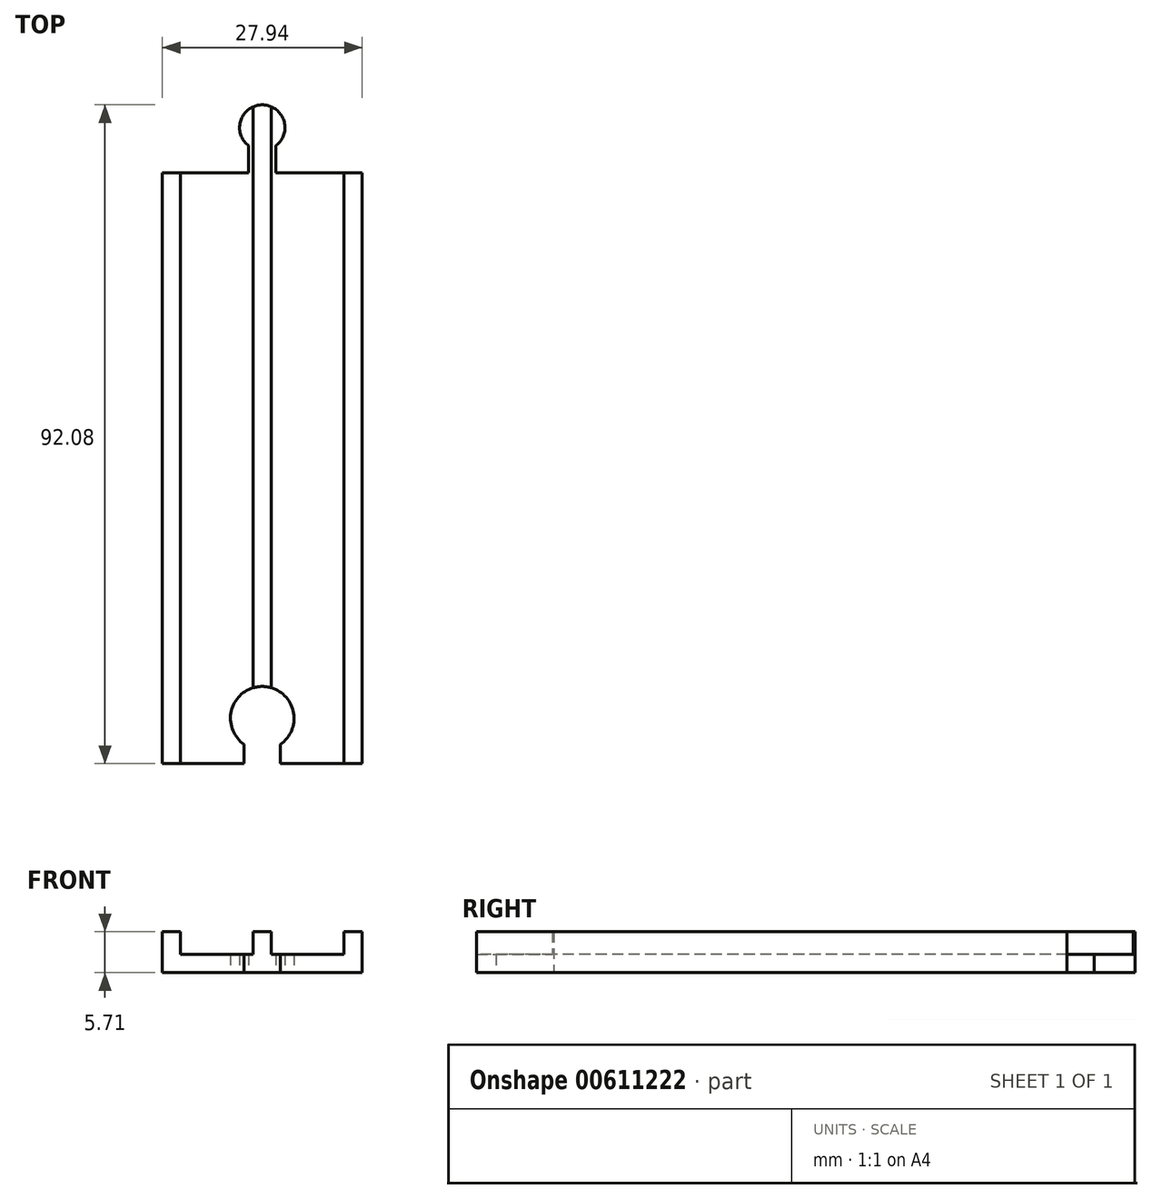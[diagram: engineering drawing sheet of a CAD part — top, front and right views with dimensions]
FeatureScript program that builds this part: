
annotation { "Feature Type Name" : "Feature", "Feature Type Description" : "" }
export const myFeature = defineFeature(function(context is Context, id is Id, definition is map)
    precondition{}
    {
        {
            var Q0;
            Q0=qCreatedBy(makeId("Top.planeOp"),FACE);
            var sketch = newSketch(context, id + "F0", { "sketchPlane" : qUnion([Q0])});
            skLineSegment(sketch, "E0.bottom", {"start": v(0, 0) * mm, "end": v(27.94, 0) * mm});
            skLineSegment(sketch, "E0.top", {"start": v(0, 82.55) * mm, "end": v(27.94, 82.55) * mm});
            skLineSegment(sketch, "E0.left", {"start": v(0, 0) * mm, "end": v(0, 82.55) * mm});
            skLineSegment(sketch, "E0.right", {"start": v(27.94, 0) * mm, "end": v(27.94, 82.55) * mm});
            skSolve(sketch);
        }
        {
            var Q0;
            Q0 = qSketchRegion(id + "F0", true);
            extrude(context, id + "F1", {"entities" : qUnion([Q0]), "depth" : 2.54 * mm, "offsetDistance" : 25.4 * mm});
        }
        {
            var Q0;
            Q0=makeQuery(id+"F1.opExtrude","CAP_FACE",FACE,{"disambiguationData":[OSD([sQuery(id+"F0.wireOp",EDGE,"E0.bottom"),sQuery(id+"F0.wireOp",EDGE,"E0.top"),sQuery(id+"F0.wireOp",EDGE,"E0.left"),sQuery(id+"F0.wireOp",EDGE,"E0.right")])],"isStart":false});
            var sketch = newSketch(context, id + "F2", { "sketchPlane" : qUnion([Q0])});
            skLineSegment(sketch, "E1.bottom", {"start": v(0, 82.55) * mm, "end": v(2.54, 82.55) * mm});
            skLineSegment(sketch, "E1.top", {"start": v(0, 0) * mm, "end": v(2.54, 0) * mm});
            skLineSegment(sketch, "E1.left", {"start": v(0, 82.55) * mm, "end": v(0, 0) * mm});
            skLineSegment(sketch, "E1.right", {"start": v(2.54, 82.55) * mm, "end": v(2.54, 0) * mm});
            skLineSegment(sketch, "E2.bottom", {"start": v(27.94, 82.55) * mm, "end": v(25.4, 82.55) * mm});
            skLineSegment(sketch, "E2.top", {"start": v(27.94, 0) * mm, "end": v(25.4, 0) * mm});
            skLineSegment(sketch, "E2.left", {"start": v(27.94, 82.55) * mm, "end": v(27.94, 0) * mm});
            skLineSegment(sketch, "E2.right", {"start": v(25.4, 82.55) * mm, "end": v(25.4, 0) * mm});
            skLineSegment(sketch, "E3", {"start": v(13.97, 82.55) * mm, "end": v(13.97, 0) * mm, "construction": true});
            skLineSegment(sketch, "E4.bottom", {"start": v(12.7, 82.55) * mm, "end": v(15.24, 82.55) * mm});
            skLineSegment(sketch, "E4.top", {"start": v(12.7, 0) * mm, "end": v(15.24, 0) * mm});
            skLineSegment(sketch, "E4.left", {"start": v(12.7, 82.55) * mm, "end": v(12.7, 0) * mm});
            skLineSegment(sketch, "E4.right", {"start": v(15.24, 82.55) * mm, "end": v(15.24, 0) * mm});
            skPoint(sketch, "E4.middle", {"position": v(13.97, 41.28) * mm});
            skSolve(sketch);
        }
        {
            var Q0;
            Q0=makeQuery(id+"F2.imprint","IMPRINT",FACE,{"disambiguationData":[TD([[makeQuery(id+"F2.imprint","IMPRINT",EDGE,{"derivedFrom":sQuery(id+"F2.wireOp",EDGE,"E1.bottom")}),-1.0]])]});
            var Q1;
            Q1=makeQuery(id+"F2.imprint","IMPRINT",FACE,{"disambiguationData":[TD([[makeQuery(id+"F2.imprint","IMPRINT",EDGE,{"derivedFrom":sQuery(id+"F2.wireOp",EDGE,"E4.bottom")}),-1.0]])]});
            var Q2;
            Q2=makeQuery(id+"F2.imprint","IMPRINT",FACE,{"disambiguationData":[TD([[makeQuery(id+"F2.imprint","IMPRINT",EDGE,{"derivedFrom":sQuery(id+"F2.wireOp",EDGE,"E2.bottom")}),-1.0]])]});
            extrude(context, id + "F3", {"entities" : qUnion([Q0, Q1, Q2]), "operationType" : NewBodyOperationType.ADD, "depth" : 3.17 * mm, "offsetDistance" : 25.4 * mm});
        }
        {
            var Q0;
            Q0=makeQuery(id+"F1.opExtrude","CAP_FACE",FACE,{"disambiguationData":[OSD([sQuery(id+"F0.wireOp",EDGE,"E0.bottom"),sQuery(id+"F0.wireOp",EDGE,"E0.top"),sQuery(id+"F0.wireOp",EDGE,"E0.left"),sQuery(id+"F0.wireOp",EDGE,"E0.right")])],"isStart":true});
            var sketch = newSketch(context, id + "F4", { "sketchPlane" : qUnion([Q0])});
            skLineSegment(sketch, "E5", {"start": v(13.97, 0) * mm, "end": v(13.97, -82.55) * mm, "construction": true});
            skArc(sketch, "E6", {"start": v(11.43, -2.7) * mm, "mid": v(13.97, -10.8) * mm, "end": v(16.51, -2.7) * mm});
            skLineSegment(sketch, "E7", {"start": v(16.51, -2.7) * mm, "end": v(16.51, 0) * mm});
            skLineSegment(sketch, "E8.MirrorCS", {"start": v(11.43, -2.7) * mm, "end": v(11.43, 0) * mm});
            skLineSegment(sketch, "E9", {"start": v(11.43, 0) * mm, "end": v(16.51, 0) * mm});
            skSolve(sketch);
        }
        {
            var Q0;
            Q0 = qSketchRegion(id + "F4", true);
            extrude(context, id + "F5", {"entities" : qUnion([Q0]), "operationType" : NewBodyOperationType.REMOVE, "oppositeDirection" : true, "depth" : 25.4 * mm, "offsetDistance" : 25.4 * mm});
        }
        {
            var Q0;
            Q0=makeQuery(id+"F1.opExtrude","CAP_FACE",FACE,{"disambiguationData":[OSD([sQuery(id+"F0.wireOp",EDGE,"E0.bottom"),sQuery(id+"F0.wireOp",EDGE,"E0.top"),sQuery(id+"F0.wireOp",EDGE,"E0.left"),sQuery(id+"F0.wireOp",EDGE,"E0.right")])],"isStart":true});
            var sketch = newSketch(context, id + "F6", { "sketchPlane" : qUnion([Q0])});
            skArc(sketch, "E10", {"start": v(12.06, -86.36) * mm, "mid": v(13.97, -92.08) * mm, "end": v(15.88, -86.36) * mm});
            skPoint(sketch, "E10.centerSnap0", {"position": v(13.97, -82.55) * mm});
            skLineSegment(sketch, "E11", {"start": v(12.06, -86.36) * mm, "end": v(12.06, -82.55) * mm});
            skLineSegment(sketch, "E12.MirrorCS", {"start": v(15.88, -86.36) * mm, "end": v(15.88, -82.55) * mm});
            skSolve(sketch);
        }
        {
            var Q0;
            Q0=makeQuery(id+"F6.imprint","IMPRINT",FACE,{"disambiguationData":[TD([[makeQuery(id+"F6.imprint","IMPRINT",EDGE,{"derivedFrom":sQuery(id+"F6.wireOp",EDGE,"E10")}),1.0]])]});
            var Q1;
            {var subQ0=sQuery(id+"F0.wireOp",EDGE,"E0.top");var subQ1=sQuery(id+"F0.wireOp",EDGE,"E0.bottom");Q1=makeQuery(id+"F3.boolean.opBoolean","SPLIT",FACE,{"disambiguationData":[TD([makeQuery(id+"F3.opExtrude","SWEPT_FACE",FACE,{"disambiguationData":[OSD([sQuery(id+"F2.wireOp",EDGE,"E1.right")])]})])],"derivedFrom":makeQuery(id+"F1.opExtrude","CAP_FACE",FACE,{"disambiguationData":[OSD([subQ1,subQ0,sQuery(id+"F0.wireOp",EDGE,"E0.left"),sQuery(id+"F0.wireOp",EDGE,"E0.right")])],"isStart":false})});}
            extrude(context, id + "F7", {"entities" : qUnion([Q0]), "operationType" : NewBodyOperationType.ADD, "endBound" : BoundingType.UP_TO_SURFACE, "oppositeDirection" : true, "depth" : 25.4 * mm, "endBoundEntityFace" : qUnion([Q1]), "offsetDistance" : 25.4 * mm});
        }
        {
            var Q0;
            {var subQ0=sQuery(id+"F2.wireOp",EDGE,"E4.left");var subQ1=sQuery(id+"F2.wireOp",EDGE,"E4.right");var subQ2=sQuery(id+"F2.wireOp",EDGE,"E4.bottom");var subQ5=sQuery(id+"F0.wireOp",EDGE,"E0.top");var subQ6=makeQuery(id+"F3.opExtrude","SWEPT_FACE",FACE,{"disambiguationData":[OSD([subQ2])]});var subQ7=makeQuery(id+"F3.opExtrude","SWEPT_FACE",FACE,{"disambiguationData":[OSD([sQuery(id+"F2.wireOp",EDGE,"E2.bottom")])]});var subQ8=makeQuery(id+"F1.opExtrude","SWEPT_FACE",FACE,{"disambiguationData":[OSD([subQ5])]});var subQ9=makeQuery(id+"F3.opExtrude","SWEPT_FACE",FACE,{"disambiguationData":[OSD([sQuery(id+"F2.wireOp",EDGE,"E1.bottom")])]});Q0=makeQuery(id+"F7.boolean.opBoolean","SPLIT",FACE,{"disambiguationData":[TD([makeQuery(id+"F3.opExtrude","CAP_FACE",FACE,{"disambiguationData":[OSD([subQ2,sQuery(id+"F2.wireOp",EDGE,"E4.top"),subQ0,subQ1])],"isStart":false})])],"derivedFrom":makeQuery(id+"F3.boolean.opBoolean","MERGE",FACE,{"derivedFrom":[subQ8,subQ9,subQ7,subQ6]})});}
            var sketch = newSketch(context, id + "F8", { "sketchPlane" : qUnion([Q0])});
            skLineSegment(sketch, "E13.bottom", {"start": v(-15.24, 5.72) * mm, "end": v(-12.7, 5.72) * mm});
            skLineSegment(sketch, "E13.top", {"start": v(-15.24, 2.54) * mm, "end": v(-12.7, 2.54) * mm});
            skLineSegment(sketch, "E13.left", {"start": v(-15.24, 5.72) * mm, "end": v(-15.24, 2.54) * mm});
            skLineSegment(sketch, "E13.right", {"start": v(-12.7, 5.72) * mm, "end": v(-12.7, 2.54) * mm});
            skSolve(sketch);
        }
        {
            var Q0;
            Q0 = qSketchRegion(id + "F8", true);
            var Q1;
            Q1=makeQuery(id+"F7.opExtrude","SWEPT_FACE",FACE,{"disambiguationData":[OSD([sQuery(id+"F6.wireOp",EDGE,"E10")])]});
            extrude(context, id + "F9", {"entities" : qUnion([Q0]), "operationType" : NewBodyOperationType.ADD, "depth" : 10.3 * mm, "endBoundEntityFace" : qUnion([Q1]), "offsetDistance" : 25.4 * mm});
        }
        {
            var Q0;
            {var subQ0=sQuery(id+"F0.wireOp",EDGE,"E0.top");Q0=makeQuery(id+"F7.boolean.opBoolean","MERGE",FACE,{"derivedFrom":[makeQuery(id+"F1.opExtrude","CAP_FACE",FACE,{"disambiguationData":[OSD([sQuery(id+"F0.wireOp",EDGE,"E0.bottom"),subQ0,sQuery(id+"F0.wireOp",EDGE,"E0.left"),sQuery(id+"F0.wireOp",EDGE,"E0.right")])],"isStart":true}),makeQuery(id+"F7.opExtrude","CAP_FACE",FACE,{"disambiguationData":[OSD([subQ0,sQuery(id+"F6.wireOp",EDGE,"E10"),sQuery(id+"F6.wireOp",EDGE,"E11"),sQuery(id+"F6.wireOp",EDGE,"E12.MirrorCS")])],"isStart":true})]});}
            var sketch = newSketch(context, id + "F10", { "sketchPlane" : qUnion([Q0])});
            skArc(sketch, "E14", {"start": v(10.8, -88.9) * mm, "mid": v(13.97, -92.08) * mm, "end": v(17.14, -88.9) * mm});
            skLineSegment(sketch, "E15", {"start": v(10.8, -88.9) * mm, "end": v(10.8, -93.87) * mm});
            skLineSegment(sketch, "E16", {"start": v(10.8, -93.87) * mm, "end": v(17.14, -93.87) * mm});
            skLineSegment(sketch, "E17", {"start": v(17.14, -93.87) * mm, "end": v(17.14, -88.9) * mm});
            skSolve(sketch);
        }
        {
            var Q0;
            Q0 = qSketchRegion(id + "F10", true);
            extrude(context, id + "F11", {"entities" : qUnion([Q0]), "operationType" : NewBodyOperationType.REMOVE, "oppositeDirection" : true, "depth" : 25.4 * mm, "offsetDistance" : 25.4 * mm});
        }
    });
